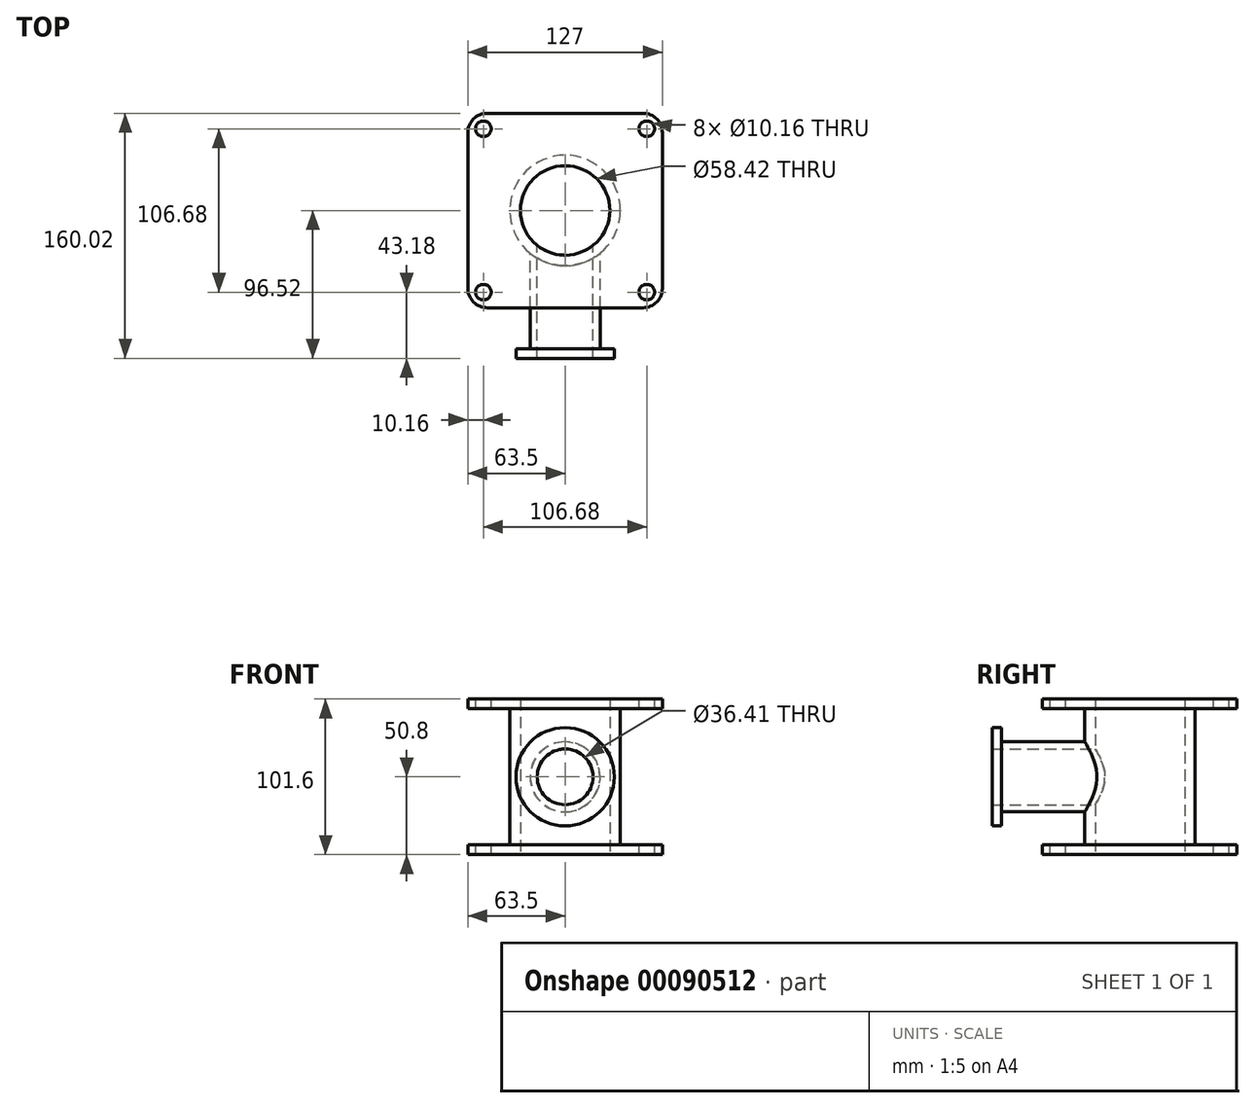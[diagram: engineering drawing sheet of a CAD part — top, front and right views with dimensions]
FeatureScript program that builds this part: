
annotation { "Feature Type Name" : "Feature", "Feature Type Description" : "" }
export const myFeature = defineFeature(function(context is Context, id is Id, definition is map)
    precondition{}
    {
        {
            var Q0;
            Q0=qCreatedBy(makeId("Top.planeOp"),FACE);
            var sketch = newSketch(context, id + "F0", { "sketchPlane" : qUnion([Q0])});
            skCircle(sketch, "E0", {"center": v(0, 0) * mm, "radius": 36.09 * mm});
            skCircle(sketch, "E1", {"center": v(0, 0) * mm, "radius": 29.21 * mm});
            skSolve(sketch);
        }
        {
            var Q0;
            Q0=makeQuery(id+"F0.imprint","IMPRINT",FACE,{"disambiguationData":[TD([[makeQuery(id+"F0.imprint","IMPRINT",EDGE,{"derivedFrom":sQuery(id+"F0.wireOp",EDGE,"E0")}),1.0]])]});
            extrude(context, id + "F1", {"entities" : qUnion([Q0]), "depth" : 50.8 * mm});
        }
        {
            var Q0;
            Q0=makeQuery(id+"F1.opExtrude","CAP_FACE",FACE,{"disambiguationData":[OSD([sQuery(id+"F0.wireOp",EDGE,"E0"),sQuery(id+"F0.wireOp",EDGE,"E1")])],"isStart":false});
            var sketch = newSketch(context, id + "F2", { "sketchPlane" : qUnion([Q0])});
            skLineSegment(sketch, "E2", {"start": v(0, 63.5) * mm, "end": v(63.5, 63.5) * mm});
            skLineSegment(sketch, "E3", {"start": v(63.5, 63.5) * mm, "end": v(63.5, 0) * mm});
            skLineSegment(sketch, "E4.MirrorCS", {"start": v(0, 63.5) * mm, "end": v(-63.5, 63.5) * mm});
            skLineSegment(sketch, "E5.MirrorCS", {"start": v(-63.5, 63.5) * mm, "end": v(-63.5, 0) * mm});
            skLineSegment(sketch, "E6.MirrorCS", {"start": v(-63.5, -63.5) * mm, "end": v(-63.5, 0) * mm});
            skLineSegment(sketch, "E7.MirrorCS", {"start": v(0, -63.5) * mm, "end": v(-63.5, -63.5) * mm});
            skLineSegment(sketch, "E8.MirrorCS", {"start": v(0, -63.5) * mm, "end": v(63.5, -63.5) * mm});
            skLineSegment(sketch, "E9.MirrorCS", {"start": v(63.5, -63.5) * mm, "end": v(63.5, 0) * mm});
            skCircle(sketch, "E10", {"center": v(0, 0) * mm, "radius": 24.5 * mm});
            skSolve(sketch);
        }
        {
            var Q0;
            Q0=makeQuery(id+"F2.imprint","IMPRINT",FACE,{"disambiguationData":[TD([[makeQuery(id+"F2.imprint","IMPRINT",EDGE,{"derivedFrom":sQuery(id+"F2.wireOp",EDGE,"E2")}),-1.0]])]});
            extrude(context, id + "F3", {"entities" : qUnion([Q0]), "oppositeDirection" : true, "depth" : 6.35 * mm});
        }
        {
            var Q0;
            Q0=makeQuery(id+"F3.opExtrude","SWEPT_BODY",BODY,{"disambiguationData":[OSD([sQuery(id+"F0.wireOp",EDGE,"E0"),sQuery(id+"F2.wireOp",EDGE,"E2"),sQuery(id+"F2.wireOp",EDGE,"E3"),sQuery(id+"F2.wireOp",EDGE,"E4.MirrorCS"),sQuery(id+"F2.wireOp",EDGE,"E5.MirrorCS"),sQuery(id+"F2.wireOp",EDGE,"E6.MirrorCS"),sQuery(id+"F2.wireOp",EDGE,"E7.MirrorCS"),sQuery(id+"F2.wireOp",EDGE,"E8.MirrorCS"),sQuery(id+"F2.wireOp",EDGE,"E9.MirrorCS")])]});
            var Q1;
            Q1=makeQuery(id+"F1.opExtrude","SWEPT_BODY",BODY,{"disambiguationData":[OSD([sQuery(id+"F0.wireOp",EDGE,"E0"),sQuery(id+"F0.wireOp",EDGE,"E1")])]});
            booleanBodies(context, id + "F4", {"operationType" : BooleanOperationType.UNION, "tools" : qUnion([Q0, Q1])});
        }
        {
            var Q0;
            Q0=makeQuery(id+"F3.opExtrude","SWEPT_BODY",BODY,{"disambiguationData":[OSD([sQuery(id+"F0.wireOp",EDGE,"E0"),sQuery(id+"F2.wireOp",EDGE,"E2"),sQuery(id+"F2.wireOp",EDGE,"E3"),sQuery(id+"F2.wireOp",EDGE,"E4.MirrorCS"),sQuery(id+"F2.wireOp",EDGE,"E5.MirrorCS"),sQuery(id+"F2.wireOp",EDGE,"E6.MirrorCS"),sQuery(id+"F2.wireOp",EDGE,"E7.MirrorCS"),sQuery(id+"F2.wireOp",EDGE,"E8.MirrorCS"),sQuery(id+"F2.wireOp",EDGE,"E9.MirrorCS")])]});
            var Q1;
            Q1=qCreatedBy(makeId("Top.planeOp"),FACE);
            mirror(context, id + "F5", {"operationType" : NewBodyOperationType.ADD, "entities" : qUnion([Q0]), "mirrorPlane" : qUnion([Q1])});
        }
        {
            var Q0;
            Q0=qCreatedBy(makeId("Front.planeOp"),FACE);
            var sketch = newSketch(context, id + "F6", { "sketchPlane" : qUnion([Q0])});
            skCircle(sketch, "E11", {"center": v(0, 0) * mm, "radius": 22.89 * mm});
            skCircle(sketch, "E12", {"center": v(0, 0) * mm, "radius": 18.2 * mm});
            skSolve(sketch);
        }
        {
            var Q0;
            Q0=makeQuery(id+"F6.imprint","IMPRINT",FACE,{"disambiguationData":[TD([[makeQuery(id+"F6.imprint","IMPRINT",EDGE,{"derivedFrom":sQuery(id+"F6.wireOp",EDGE,"E11")}),1.0]])]});
            extrude(context, id + "F7", {"entities" : qUnion([Q0]), "operationType" : NewBodyOperationType.ADD, "depth" : 96.52 * mm});
        }
        {
            var Q0;
            Q0=makeQuery(id+"F6.imprint","IMPRINT",FACE,{"disambiguationData":[TD([[makeQuery(id+"F6.imprint","IMPRINT",EDGE,{"derivedFrom":sQuery(id+"F6.wireOp",EDGE,"E12")}),1.0]])]});
            extrude(context, id + "F8", {"entities" : qUnion([Q0]), "operationType" : NewBodyOperationType.REMOVE, "depth" : 76.2 * mm});
        }
        {
            var Q0;
            {var subQ0=sQuery(id+"F0.wireOp",EDGE,"E0");Q0=makeQuery(id+"F4.opBoolean","MERGE",FACE,{"derivedFrom":[makeQuery(id+"F1.opExtrude","CAP_FACE",FACE,{"disambiguationData":[OSD([subQ0,sQuery(id+"F0.wireOp",EDGE,"E1")])],"isStart":false}),makeQuery(id+"F3.opExtrude","CAP_FACE",FACE,{"disambiguationData":[OSD([subQ0,sQuery(id+"F2.wireOp",EDGE,"E2"),sQuery(id+"F2.wireOp",EDGE,"E3"),sQuery(id+"F2.wireOp",EDGE,"E4.MirrorCS"),sQuery(id+"F2.wireOp",EDGE,"E5.MirrorCS"),sQuery(id+"F2.wireOp",EDGE,"E6.MirrorCS"),sQuery(id+"F2.wireOp",EDGE,"E7.MirrorCS"),sQuery(id+"F2.wireOp",EDGE,"E8.MirrorCS"),sQuery(id+"F2.wireOp",EDGE,"E9.MirrorCS")])],"isStart":true})]});}
            var sketch = newSketch(context, id + "F9", { "sketchPlane" : qUnion([Q0])});
            skPoint(sketch, "E13", {"position": v(0, 0) * mm});
            skSolve(sketch);
        }
        {
            var Q0;
            Q0=sQuery(id+"F9.wireOp",VERTEX,"E13");
            var Q1;
            Q1=makeQuery(id+"F3.opExtrude","SWEPT_BODY",BODY,{"disambiguationData":[OSD([sQuery(id+"F0.wireOp",EDGE,"E0"),sQuery(id+"F2.wireOp",EDGE,"E2"),sQuery(id+"F2.wireOp",EDGE,"E3"),sQuery(id+"F2.wireOp",EDGE,"E4.MirrorCS"),sQuery(id+"F2.wireOp",EDGE,"E5.MirrorCS"),sQuery(id+"F2.wireOp",EDGE,"E6.MirrorCS"),sQuery(id+"F2.wireOp",EDGE,"E7.MirrorCS"),sQuery(id+"F2.wireOp",EDGE,"E8.MirrorCS"),sQuery(id+"F2.wireOp",EDGE,"E9.MirrorCS")])]});
            hole(context, id + "F10", {"style" : HoleStyle.SIMPLE, "endStyle" : HoleEndStyle.BLIND, "holeDiameter" : 58.42 * mm, "holeDepth" : 101.6 * mm, "locations" : qUnion([Q0]), "scope" : qUnion([Q1])});
        }
        {
            var Q0;
            Q0=makeQuery(id+"F7.opExtrude","CAP_FACE",FACE,{"disambiguationData":[OSD([sQuery(id+"F6.wireOp",EDGE,"E11"),sQuery(id+"F6.wireOp",EDGE,"E12")])],"isStart":false});
            var sketch = newSketch(context, id + "F11", { "sketchPlane" : qUnion([Q0])});
            skCircle(sketch, "E14", {"center": v(0, 0) * mm, "radius": 32.12 * mm});
            skCircle(sketch, "E15", {"center": v(0, 0) * mm, "radius": 18.1 * mm});
            skSolve(sketch);
        }
        {
            var Q0;
            Q0=makeQuery(id+"F11.imprint","IMPRINT",FACE,{"disambiguationData":[TD([[makeQuery(id+"F11.imprint","IMPRINT",EDGE,{"derivedFrom":sQuery(id+"F11.wireOp",EDGE,"E14")}),1.0]])]});
            var Q1;
            Q1=makeQuery(id+"F11.imprint","IMPRINT",FACE,{"disambiguationData":[TD([[makeQuery(id+"F11.imprint","IMPRINT",EDGE,{"derivedFrom":makeQuery(id+"F7.opExtrude","CAP_EDGE",EDGE,{"disambiguationData":[OSD([sQuery(id+"F6.wireOp",EDGE,"E11")])],"isStart":false})}),1.0]])]});
            extrude(context, id + "F12", {"entities" : qUnion([Q0, Q1]), "operationType" : NewBodyOperationType.ADD, "oppositeDirection" : true, "depth" : 6.35 * mm});
        }
        {
            var Q0;
            {var subQ0=sQuery(id+"F0.wireOp",EDGE,"E0");Q0=makeQuery(id+"F4.opBoolean","MERGE",FACE,{"derivedFrom":[makeQuery(id+"F1.opExtrude","CAP_FACE",FACE,{"disambiguationData":[OSD([subQ0,sQuery(id+"F0.wireOp",EDGE,"E1")])],"isStart":false}),makeQuery(id+"F3.opExtrude","CAP_FACE",FACE,{"disambiguationData":[OSD([subQ0,sQuery(id+"F2.wireOp",EDGE,"E2"),sQuery(id+"F2.wireOp",EDGE,"E3"),sQuery(id+"F2.wireOp",EDGE,"E4.MirrorCS"),sQuery(id+"F2.wireOp",EDGE,"E5.MirrorCS"),sQuery(id+"F2.wireOp",EDGE,"E6.MirrorCS"),sQuery(id+"F2.wireOp",EDGE,"E7.MirrorCS"),sQuery(id+"F2.wireOp",EDGE,"E8.MirrorCS"),sQuery(id+"F2.wireOp",EDGE,"E9.MirrorCS")])],"isStart":true})]});}
            var sketch = newSketch(context, id + "F13", { "sketchPlane" : qUnion([Q0])});
            skPoint(sketch, "E16", {"position": v(53.34, 53.34) * mm});
            skPoint(sketch, "E17.MirrorP", {"position": v(53.34, -53.34) * mm});
            skPoint(sketch, "E18.MirrorP", {"position": v(-53.34, 53.34) * mm});
            skPoint(sketch, "E19.MirrorP", {"position": v(-53.34, -53.34) * mm});
            skSolve(sketch);
        }
        {
            var Q0;
            Q0=sQuery(id+"F13.wireOp",VERTEX,"E16");
            var Q1;
            Q1=sQuery(id+"F13.wireOp",VERTEX,"E17.MirrorP");
            var Q2;
            Q2=sQuery(id+"F13.wireOp",VERTEX,"E19.MirrorP");
            var Q3;
            Q3=sQuery(id+"F13.wireOp",VERTEX,"E18.MirrorP");
            var Q4;
            Q4=makeQuery(id+"F3.opExtrude","SWEPT_BODY",BODY,{"disambiguationData":[OSD([sQuery(id+"F0.wireOp",EDGE,"E0"),sQuery(id+"F2.wireOp",EDGE,"E2"),sQuery(id+"F2.wireOp",EDGE,"E3"),sQuery(id+"F2.wireOp",EDGE,"E4.MirrorCS"),sQuery(id+"F2.wireOp",EDGE,"E5.MirrorCS"),sQuery(id+"F2.wireOp",EDGE,"E6.MirrorCS"),sQuery(id+"F2.wireOp",EDGE,"E7.MirrorCS"),sQuery(id+"F2.wireOp",EDGE,"E8.MirrorCS"),sQuery(id+"F2.wireOp",EDGE,"E9.MirrorCS")])]});
            hole(context, id + "F14", {"style" : HoleStyle.SIMPLE, "endStyle" : HoleEndStyle.THROUGH, "holeDiameter" : 10.16 * mm, "locations" : qUnion([Q0, Q1, Q2, Q3]), "scope" : qUnion([Q4]), "isTappedThrough" : true});
        }
        {
            var Q0;
            Q0=makeQuery(id+"F5.opPattern","COPY",EDGE,{"derivedFrom":makeQuery(id+"F3.opExtrude","SWEPT_EDGE",EDGE,{"disambiguationData":[OSD([sQuery(id+"F2.wireOp",EDGE,"E4.MirrorCS"),sQuery(id+"F2.wireOp",EDGE,"E5.MirrorCS")])]}),"instanceName":"1"});
            var Q1;
            Q1=makeQuery(id+"F3.opExtrude","SWEPT_EDGE",EDGE,{"disambiguationData":[OSD([sQuery(id+"F2.wireOp",EDGE,"E4.MirrorCS"),sQuery(id+"F2.wireOp",EDGE,"E5.MirrorCS")])]});
            var Q2;
            Q2=makeQuery(id+"F5.opPattern","COPY",EDGE,{"derivedFrom":makeQuery(id+"F3.opExtrude","SWEPT_EDGE",EDGE,{"disambiguationData":[OSD([sQuery(id+"F2.wireOp",EDGE,"E6.MirrorCS"),sQuery(id+"F2.wireOp",EDGE,"E7.MirrorCS")])]}),"instanceName":"1"});
            var Q3;
            Q3=makeQuery(id+"F3.opExtrude","SWEPT_EDGE",EDGE,{"disambiguationData":[OSD([sQuery(id+"F2.wireOp",EDGE,"E6.MirrorCS"),sQuery(id+"F2.wireOp",EDGE,"E7.MirrorCS")])]});
            var Q4;
            Q4=makeQuery(id+"F3.opExtrude","SWEPT_EDGE",EDGE,{"disambiguationData":[OSD([sQuery(id+"F2.wireOp",EDGE,"E8.MirrorCS"),sQuery(id+"F2.wireOp",EDGE,"E9.MirrorCS")])]});
            var Q5;
            Q5=makeQuery(id+"F5.opPattern","COPY",EDGE,{"derivedFrom":makeQuery(id+"F3.opExtrude","SWEPT_EDGE",EDGE,{"disambiguationData":[OSD([sQuery(id+"F2.wireOp",EDGE,"E8.MirrorCS"),sQuery(id+"F2.wireOp",EDGE,"E9.MirrorCS")])]}),"instanceName":"1"});
            var Q6;
            Q6=makeQuery(id+"F3.opExtrude","SWEPT_EDGE",EDGE,{"disambiguationData":[OSD([sQuery(id+"F2.wireOp",EDGE,"E2"),sQuery(id+"F2.wireOp",EDGE,"E3")])]});
            var Q7;
            Q7=makeQuery(id+"F5.opPattern","COPY",EDGE,{"derivedFrom":makeQuery(id+"F3.opExtrude","SWEPT_EDGE",EDGE,{"disambiguationData":[OSD([sQuery(id+"F2.wireOp",EDGE,"E2"),sQuery(id+"F2.wireOp",EDGE,"E3")])]}),"instanceName":"1"});
            fillet(context, id + "F15", {"entities" : qUnion([Q0, Q1, Q2, Q3, Q4, Q5, Q6, Q7]), "radius" : 12.7 * mm, "tangentPropagation" : true, "allowEdgeOverflow" : false});
        }
    });
